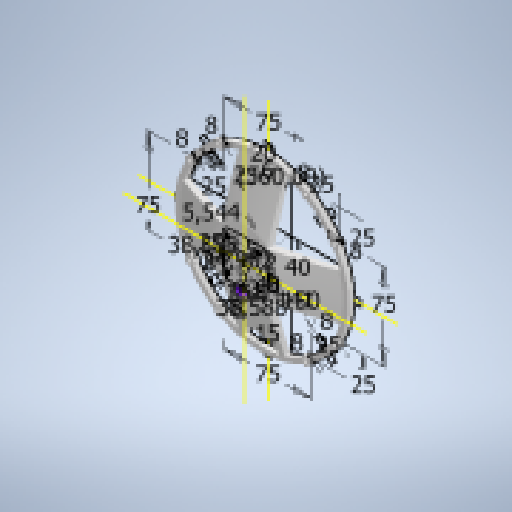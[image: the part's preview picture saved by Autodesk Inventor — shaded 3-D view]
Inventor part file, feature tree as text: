
AUTODESK INVENTOR PART (.ipt)
format: ipt  version: 2024.3 (Build 283343000, 343)  size: 372,224 bytes
history: native  units: in
note: dims shown in document units (in); Inventor stores cm internally (conversion verified against a paired STEP export)
features: sketch x4, extrude x4, chamfer x4, hole x2, revolve x1
ambient origin geometry x8: Origin, YZ Plane, XZ Plane, XY Plane, X Axis, Y Axis, Z Axis, Center Point
bodies: Solid1 (feature_tree)
feature tree (15):
  sketch  "Sketch1"  dims[d1=3.1496in d2=5.5512in d3=5.9055in d4=0.2362in d5=0.7874in d6=360.0deg d7=0.9843in d8=0.9843in d9=2.9528in d10=0.9843in d11=0.9843in d12=0.9843in d13=0.9843in d14=2.9528in d15=0.9843in d16=0.9843in d17=2.9528in d18=2.9528in d19=0.315in d20=0.315in d21=0.315in d22=0.315in d23=0.315in d24=0.315in d25=0.315in d26=0.315in d27=0.1969in d28=0.0in]
  extrude  "Extrusion1"  Depth=0.1969in TaperAngle=0.0deg
  hole  "Hole1"  [1 undecoded]
  extrude  "Extrusion2"  Depth=0.7874in TaperAngle=0.0deg
  extrude  "Extrusion3"  Depth=0.1969in
  sketch  "Sketch2"  dims[d29=0.126in d30=0.2362in d31=0.1575in d32=0.0787in d33=90.0deg d34=0.315in d35=0.8108in d36=1.5748in]
  extrude  "Extrusion4"  Depth=0.1969in
  chamfer  "Chamfer1"  Distance=0.689in
  chamfer  "Chamfer2"  Distance=0.5906in
  chamfer  "Chamfer3"  Distance=0.7874in
  chamfer  "Chamfer4"  Distance=1.6535in Angle=45.0deg
  revolve  "Revolution1"  Angle=45.0deg
  hole  "Hole2"  [1 undecoded]
  sketch  "Sketch3"  dims[d37=1.5748in d38=0.7874in d39=0.0in]
  sketch  "Sketch4"  dims[d40=0.1969in d41=0.0in d42=0.1969in d43=0.1969in d44=0.689in d45=0.5906in d46=0.7874in d47=0.0in d48=1.6535in d49=0.5906in d50=45.0deg d51=1.6535in d52=0.5906in d53=45.0deg d54=1.6535in d55=0.5906in d56=45.0deg d57=1.6535in d58=0.5906in d59=45.0deg d60=2.7756in d61=360.0deg d62=0.5906in d63=0.9843in d64=1.5192in d65=1.5192in d66=0.2183in d67=0.2835in d68=0.9213in d69=0.2835in d70=0.9804in d71=1.9608in d72=0.3346in d73=0.126in d74=0.2362in d75=0.1575in d76=0.0787in d77=90.0deg d78=0.315in d79=0.8108in]
note: 2 required parameter values undecoded (feature->parameter linkage not recoverable at this tier; creation-order binding heuristic only, values carry confidence <= 0.55)
